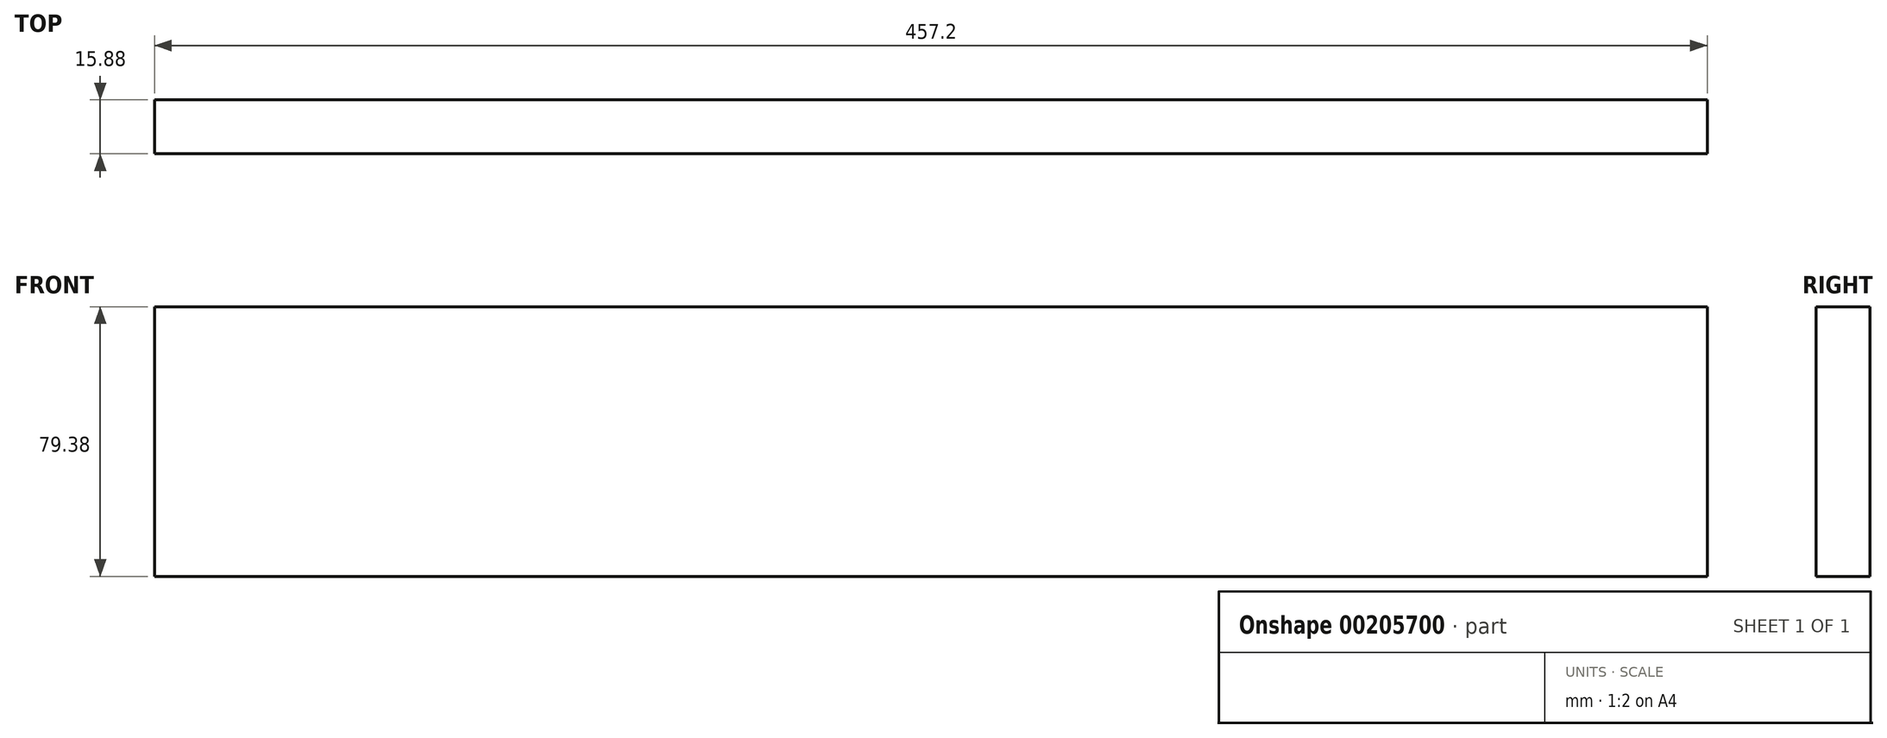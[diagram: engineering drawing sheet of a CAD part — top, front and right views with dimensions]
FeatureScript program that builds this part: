
annotation { "Feature Type Name" : "Feature", "Feature Type Description" : "" }
export const myFeature = defineFeature(function(context is Context, id is Id, definition is map)
    precondition{}
    {
        {
            var Q0;
            Q0=qCreatedBy(makeId("Front.planeOp"),FACE);
            var sketch = newSketch(context, id + "F0", { "sketchPlane" : qUnion([Q0])});
            skLineSegment(sketch, "E0.bottom", {"start": v(228.6, -39.69) * mm, "end": v(-228.6, -39.69) * mm});
            skLineSegment(sketch, "E0.top", {"start": v(228.6, 39.69) * mm, "end": v(-228.6, 39.69) * mm});
            skLineSegment(sketch, "E0.left", {"start": v(228.6, -39.69) * mm, "end": v(228.6, 39.69) * mm});
            skLineSegment(sketch, "E0.right", {"start": v(-228.6, -39.69) * mm, "end": v(-228.6, 39.69) * mm});
            skPoint(sketch, "E0.middle", {"position": v(0, 0) * mm});
            skSolve(sketch);
        }
        {
            var Q0;
            Q0=makeQuery(id+"F0.imprint","IMPRINT",FACE,{"disambiguationData":[TD([[makeQuery(id+"F0.imprint","IMPRINT",EDGE,{"derivedFrom":sQuery(id+"F0.wireOp",EDGE,"E0.bottom")}),-1.0]])]});
            extrude(context, id + "F1", {"entities" : qUnion([Q0]), "depth" : 15.88 * mm});
        }
    });
